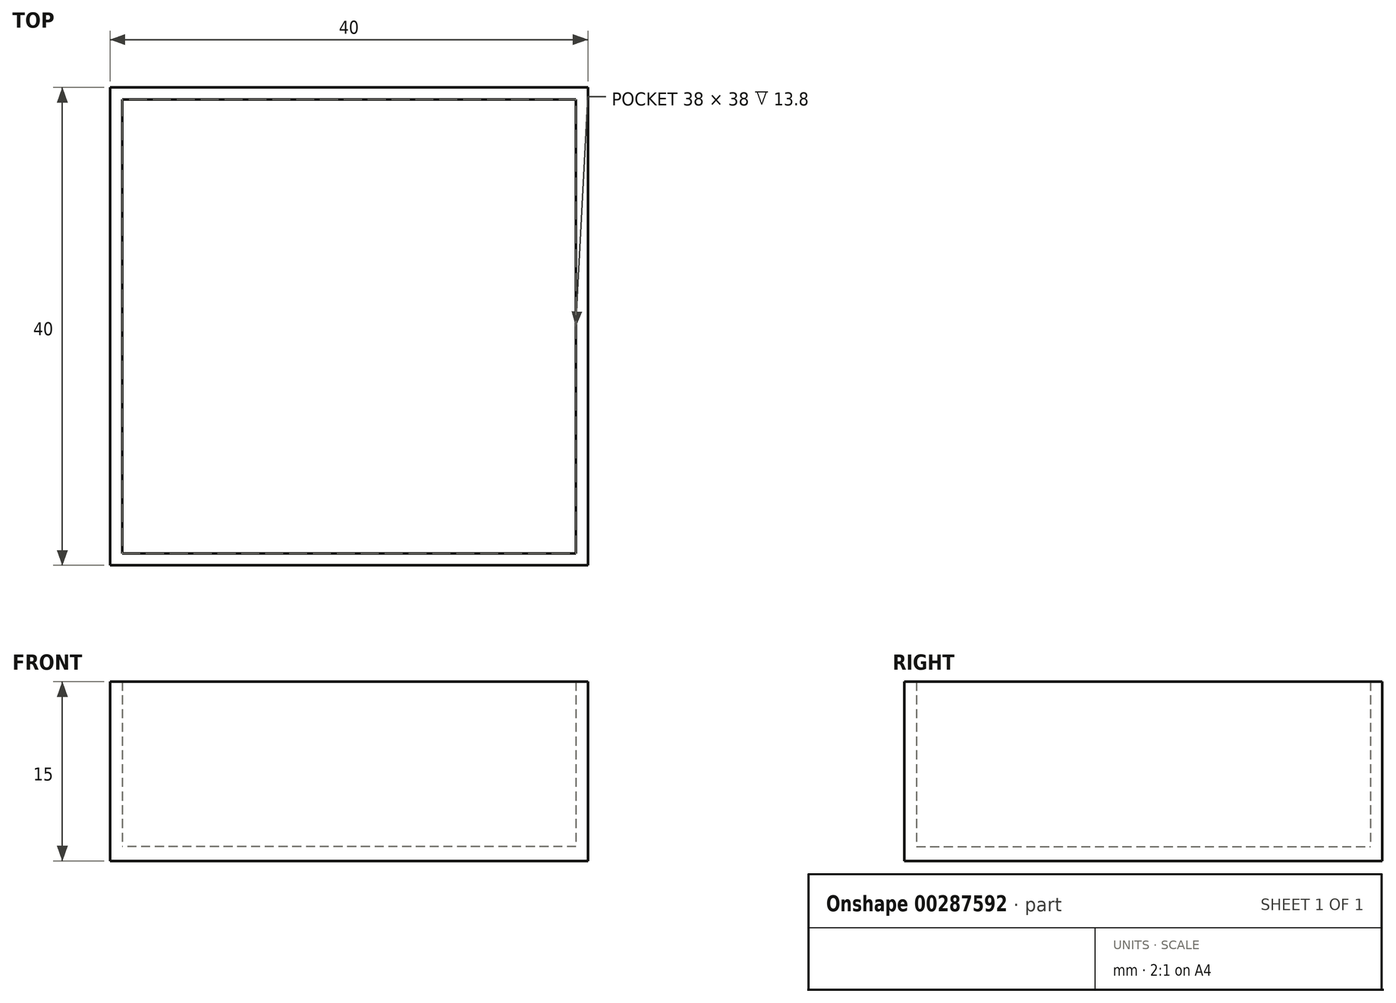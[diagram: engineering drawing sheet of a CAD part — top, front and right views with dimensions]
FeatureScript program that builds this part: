
annotation { "Feature Type Name" : "Feature", "Feature Type Description" : "" }
export const myFeature = defineFeature(function(context is Context, id is Id, definition is map)
    precondition{}
    {
        {
            assignVariable(context, id + "F0", {"name" : "layer_height", "anyValue" : 0.2});
        }
        {
            var Q0;
            Q0=qCreatedBy(makeId("Top.planeOp"),FACE);
            var sketch = newSketch(context, id + "F1", { "sketchPlane" : qUnion([Q0])});
            skLineSegment(sketch, "E0.bottom", {"start": v(20, -20) * mm, "end": v(-20, -20) * mm});
            skLineSegment(sketch, "E0.top", {"start": v(20, 20) * mm, "end": v(-20, 20) * mm});
            skLineSegment(sketch, "E0.left", {"start": v(20, -20) * mm, "end": v(20, 20) * mm});
            skLineSegment(sketch, "E0.right", {"start": v(-20, -20) * mm, "end": v(-20, 20) * mm});
            skPoint(sketch, "E0.middle", {"position": v(0, 0) * mm});
            skLineSegment(sketch, "E1.bottom", {"start": v(19, -19) * mm, "end": v(-19, -19) * mm});
            skLineSegment(sketch, "E1.top", {"start": v(19, 19) * mm, "end": v(-19, 19) * mm});
            skLineSegment(sketch, "E1.left", {"start": v(19, -19) * mm, "end": v(19, 19) * mm});
            skLineSegment(sketch, "E1.right", {"start": v(-19, -19) * mm, "end": v(-19, 19) * mm});
            skSolve(sketch);
        }
        {
            var Q0;
            Q0 = qSketchRegion(id + "F1", true);
            extrude(context, id + "F2", {"entities" : qUnion([Q0]), "depth" : 15 * mm, "offsetDistance" : 25 * mm});
        }
        {
            var Q0;
            Q0=makeQuery(id+"F1.imprint","IMPRINT",FACE,{"disambiguationData":[TD([[makeQuery(id+"F1.imprint","IMPRINT",EDGE,{"derivedFrom":sQuery(id+"F1.wireOp",EDGE,"E1.bottom")}),-1.0]])]});
            extrude(context, id + "F3", {"entities" : qUnion([Q0]), "operationType" : NewBodyOperationType.ADD, "depth" : (6 * getVariable(context, 'layer_height')) * mm, "offsetDistance" : 25 * mm});
        }
    });
